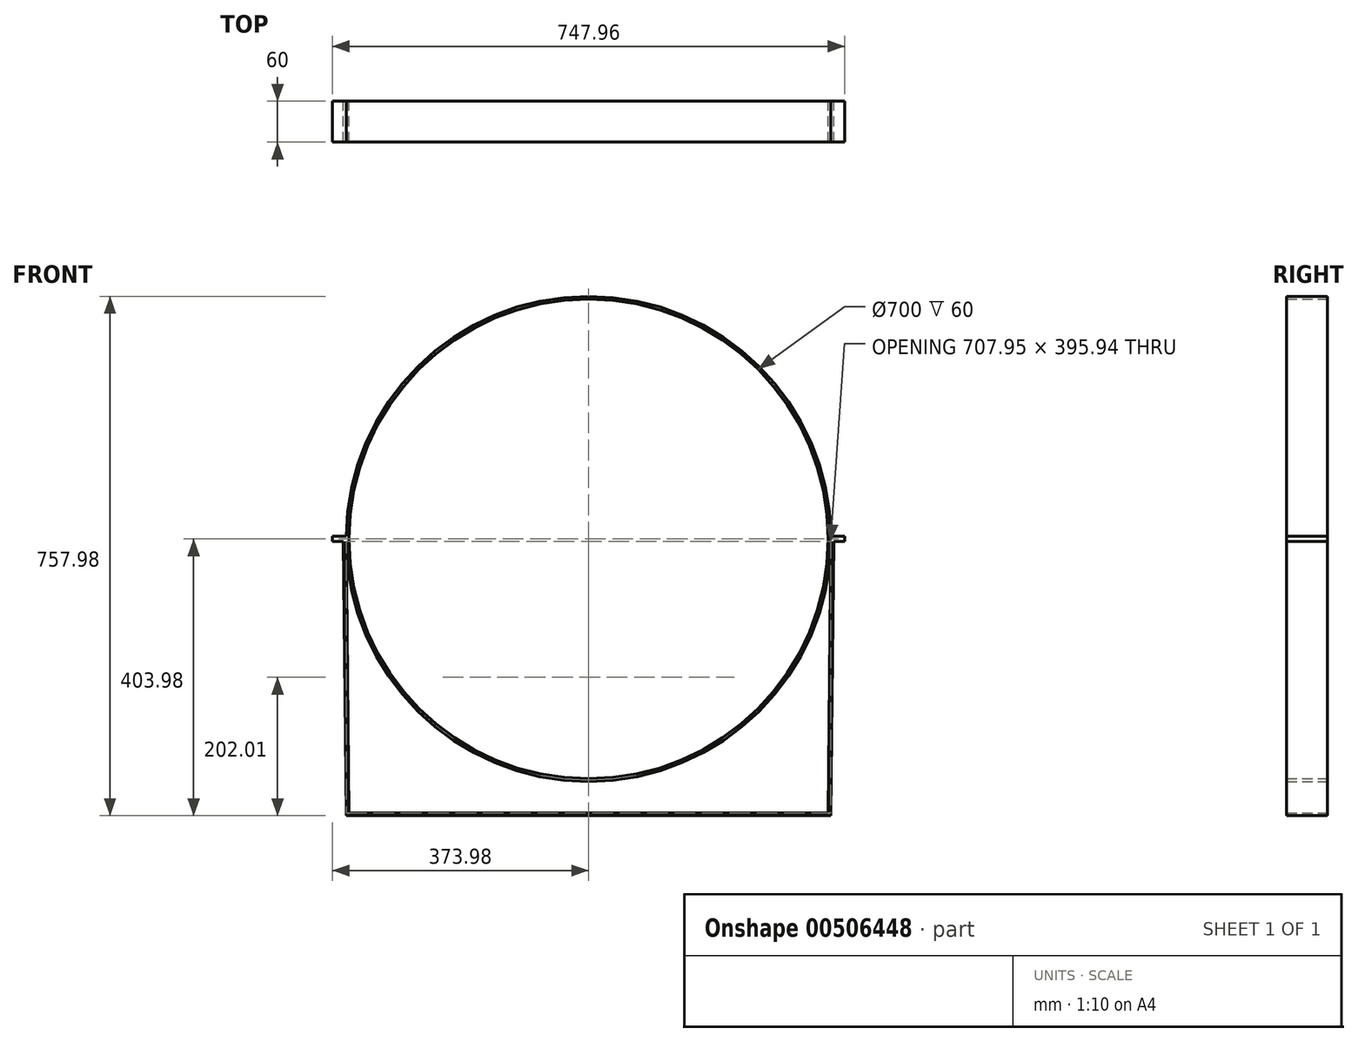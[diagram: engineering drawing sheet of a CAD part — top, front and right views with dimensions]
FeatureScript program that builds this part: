
annotation { "Feature Type Name" : "Feature", "Feature Type Description" : "" }
export const myFeature = defineFeature(function(context is Context, id is Id, definition is map)
    precondition{}
    {
        {
            var Q0;
            Q0=qCreatedBy(makeId("Front.planeOp"),FACE);
            var sketch = newSketch(context, id + "F0", { "sketchPlane" : qUnion([Q0])});
            skCircle(sketch, "E0", {"center": v(0, 0) * mm, "radius": 350 * mm});
            skCircle(sketch, "E1", {"center": v(0, 0) * mm, "radius": 354 * mm});
            skLineSegment(sketch, "E2", {"start": v(0, 0) * mm, "end": v(-690.21, 0) * mm, "construction": true});
            skLineSegment(sketch, "E3", {"start": v(-353.98, 4) * mm, "end": v(-373.98, 4) * mm});
            skLineSegment(sketch, "E4", {"start": v(-373.98, 4) * mm, "end": v(-373.98, 0) * mm});
            skLineSegment(sketch, "E5.MirrorCS", {"start": v(-353.98, -4) * mm, "end": v(-373.98, -4) * mm});
            skLineSegment(sketch, "E6.MirrorCS", {"start": v(-373.98, -4) * mm, "end": v(-373.98, 0) * mm});
            skLineSegment(sketch, "E7", {"start": v(0, 0) * mm, "end": v(0, 668.71) * mm, "construction": true});
            skLineSegment(sketch, "E8.MirrorCS", {"start": v(373.98, 4) * mm, "end": v(373.98, 0) * mm});
            skLineSegment(sketch, "E9.MirrorCS", {"start": v(373.98, -4) * mm, "end": v(373.98, 0) * mm});
            skLineSegment(sketch, "E10.MirrorCS", {"start": v(353.98, 4) * mm, "end": v(373.98, 4) * mm});
            skLineSegment(sketch, "E11.MirrorCS", {"start": v(353.98, -4) * mm, "end": v(373.98, -4) * mm});
            skLineSegment(sketch, "E12", {"start": v(-353.98, -4) * mm, "end": v(-357.98, -4) * mm});
            skLineSegment(sketch, "E13", {"start": v(-357.98, -4) * mm, "end": v(-353.98, -403.98) * mm});
            skLineSegment(sketch, "E14", {"start": v(-353.98, -4) * mm, "end": v(-350.02, -399.94) * mm});
            skLineSegment(sketch, "E15.MirrorCS", {"start": v(353.98, -4) * mm, "end": v(350.02, -399.94) * mm});
            skLineSegment(sketch, "E16.MirrorCS", {"start": v(357.98, -4) * mm, "end": v(353.98, -403.98) * mm});
            skLineSegment(sketch, "E17", {"start": v(-353.98, -403.98) * mm, "end": v(353.98, -403.98) * mm});
            skLineSegment(sketch, "E18", {"start": v(-350.02, -399.94) * mm, "end": v(350.02, -399.94) * mm});
            skSolve(sketch);
        }
        {
            var Q0;
            Q0=qSketchRegion(id+"F0",true);
            extrude(context, id + "F1", {"entities" : qUnion([Q0]), "offsetDistance" : 25 * mm, "depth" : 60 * mm});
        }
    });
